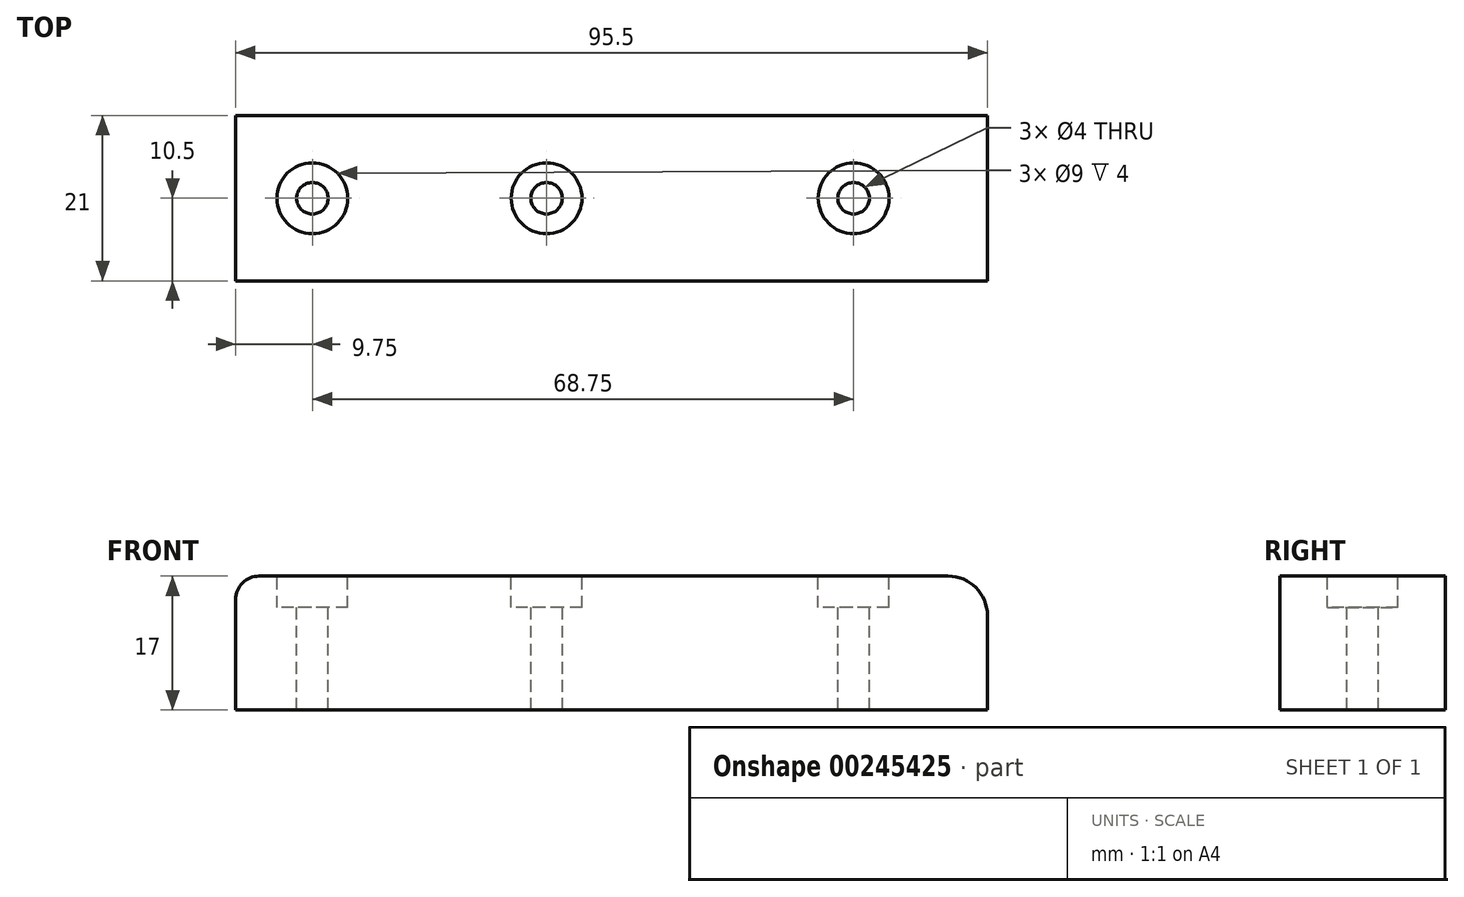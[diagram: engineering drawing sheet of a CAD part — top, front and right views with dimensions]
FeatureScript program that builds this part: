
annotation { "Feature Type Name" : "Feature", "Feature Type Description" : "" }
export const myFeature = defineFeature(function(context is Context, id is Id, definition is map)
    precondition{}
    {
        {
            var Q0;
            Q0=qCreatedBy(makeId("Front.planeOp"),FACE);
            var sketch = newSketch(context, id + "F0", { "sketchPlane" : qUnion([Q0])});
            skLineSegment(sketch, "E0.top", {"start": v(6.9, 17) * mm, "end": v(95.5, 17) * mm});
            skLineSegment(sketch, "E0.right", {"start": v(95.5, 0) * mm, "end": v(95.5, 17) * mm});
            skLineSegment(sketch, "E1", {"start": v(6.9, 17) * mm, "end": v(0, 17) * mm});
            skLineSegment(sketch, "E2", {"start": v(0, 17) * mm, "end": v(0, 0) * mm});
            skLineSegment(sketch, "E3", {"start": v(0, 0) * mm, "end": v(95.5, 0) * mm});
            skSolve(sketch);
        }
        {
            var Q0;
            Q0=qSketchRegion(id+"F0",true);
            extrude(context, id + "F1", {"entities" : qUnion([Q0]), "depth" : 21 * mm});
        }
        {
            var Q0;
            Q0=makeQuery(id+"F1.opExtrude","SWEPT_EDGE",EDGE,{"disambiguationData":[OSD([sQuery(id+"F0.wireOp",EDGE,"E0.top"),sQuery(id+"F0.wireOp",EDGE,"E0.right")])]});
            fillet(context, id + "F2", {"entities" : qUnion([Q0]), "radius" : 5 * mm, "tangentPropagation" : true, "allowEdgeOverflow" : false});
        }
        {
            var Q0;
            Q0=makeQuery(id+"F1.opExtrude","SWEPT_FACE",FACE,{"disambiguationData":[OSD([sQuery(id+"F0.wireOp",EDGE,"E0.top"),sQuery(id+"F0.wireOp",EDGE,"E1")])]});
            var sketch = newSketch(context, id + "F3", { "sketchPlane" : qUnion([Q0])});
            skLineSegment(sketch, "E4", {"start": v(0, -10.5) * mm, "end": v(19.5, -10.5) * mm});
            skLineSegment(sketch, "E5", {"start": v(19.5, -10.5) * mm, "end": v(39.5, -10.5) * mm});
            skLineSegment(sketch, "E6", {"start": v(90.5, -10.5) * mm, "end": v(78.5, -10.5) * mm});
            skCircle(sketch, "E7", {"center": v(9.75, -10.5) * mm, "radius": 2 * mm});
            skCircle(sketch, "E8", {"center": v(39.5, -10.5) * mm, "radius": 2 * mm});
            skCircle(sketch, "E9", {"center": v(78.5, -10.5) * mm, "radius": 2 * mm});
            skSolve(sketch);
        }
        {
            var Q0;
            Q0=qSketchRegion(id+"F3",true);
            extrude(context, id + "F4", {"entities" : qUnion([Q0]), "operationType" : NewBodyOperationType.REMOVE, "oppositeDirection" : true, "depth" : 25 * mm});
        }
        {
            var Q0;
            Q0=makeQuery(id+"F1.opExtrude","SWEPT_FACE",FACE,{"disambiguationData":[OSD([sQuery(id+"F0.wireOp",EDGE,"E0.top"),sQuery(id+"F0.wireOp",EDGE,"E1")])]});
            var sketch = newSketch(context, id + "F5", { "sketchPlane" : qUnion([Q0])});
            skCircle(sketch, "E10", {"center": v(9.75, -10.5) * mm, "radius": 4.5 * mm});
            skCircle(sketch, "E11", {"center": v(39.5, -10.5) * mm, "radius": 4.5 * mm});
            skCircle(sketch, "E12", {"center": v(78.5, -10.5) * mm, "radius": 4.5 * mm});
            skSolve(sketch);
        }
        {
            var Q0;
            Q0=qSketchRegion(id+"F5",true);
            extrude(context, id + "F6", {"entities" : qUnion([Q0]), "operationType" : NewBodyOperationType.REMOVE, "oppositeDirection" : true, "depth" : 4 * mm});
        }
        {
            var Q0;
            Q0=makeQuery(id+"F1.opExtrude","SWEPT_EDGE",EDGE,{"disambiguationData":[OSD([sQuery(id+"F0.wireOp",EDGE,"E1"),sQuery(id+"F0.wireOp",EDGE,"E2")])]});
            fillet(context, id + "F7", {"entities" : qUnion([Q0]), "radius" : 3 * mm, "tangentPropagation" : true, "allowEdgeOverflow" : false});
        }
    });
